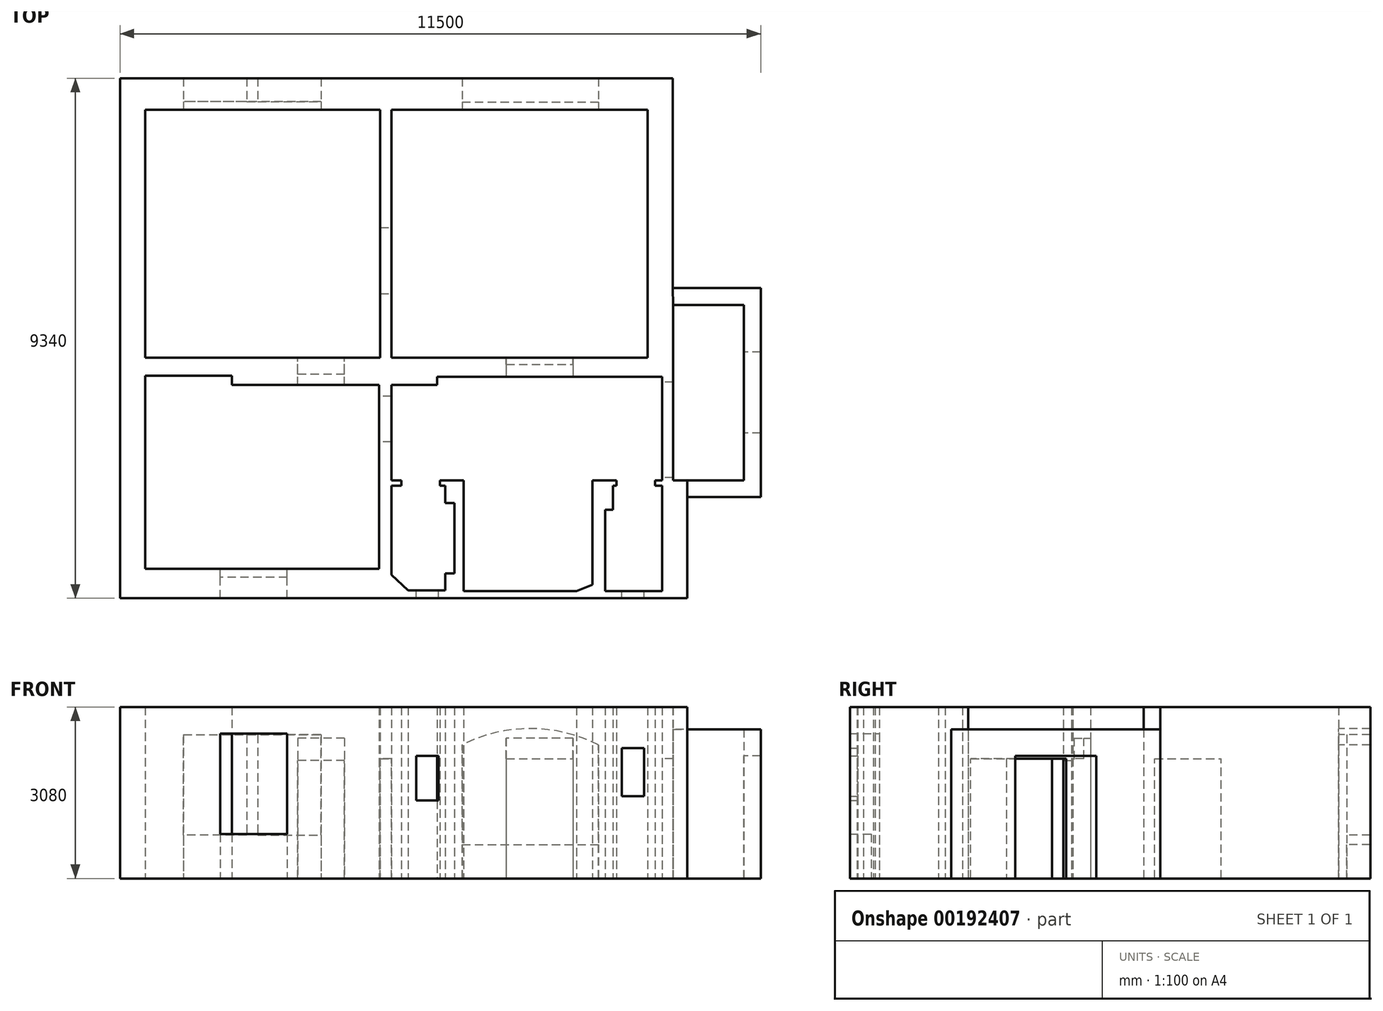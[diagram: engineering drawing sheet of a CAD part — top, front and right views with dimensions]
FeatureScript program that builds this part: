
annotation { "Feature Type Name" : "Feature", "Feature Type Description" : "" }
export const myFeature = defineFeature(function(context is Context, id is Id, definition is map)
    precondition{}
    {
        {
            var Q0;
            Q0=qCreatedBy(makeId("Top.planeOp"),FACE);
            var sketch = newSketch(context, id + "F0", { "sketchPlane" : qUnion([Q0])});
            skLineSegment(sketch, "E0.bottom", {"start": v(0, 0) * mm, "end": v(4600, 0) * mm});
            skLineSegment(sketch, "E0.top", {"start": v(0, 4450) * mm, "end": v(4600, 4450) * mm});
            skLineSegment(sketch, "E0.left", {"start": v(0, 0) * mm, "end": v(0, 4450) * mm});
            skLineSegment(sketch, "E0.right", {"start": v(4600, 0) * mm, "end": v(4600, 4450) * mm});
            skLineSegment(sketch, "E1.bottom", {"start": v(-200, 0) * mm, "end": v(-4420, 0) * mm});
            skLineSegment(sketch, "E1.top", {"start": v(-200, 4450) * mm, "end": v(-4420, 4450) * mm});
            skLineSegment(sketch, "E1.left", {"start": v(-200, 0) * mm, "end": v(-200, 4450) * mm});
            skLineSegment(sketch, "E1.right", {"start": v(-4420, 0) * mm, "end": v(-4420, 4450) * mm});
            skLineSegment(sketch, "E2", {"start": v(-220, -490) * mm, "end": v(-220, -3790) * mm});
            skLineSegment(sketch, "E3", {"start": v(-220, -3790) * mm, "end": v(-4420, -3790) * mm});
            skLineSegment(sketch, "E4", {"start": v(-4420, -3790) * mm, "end": v(-4420, -320) * mm});
            skLineSegment(sketch, "E5", {"start": v(-4420, -320) * mm, "end": v(-2860, -320) * mm});
            skLineSegment(sketch, "E6", {"start": v(-2860, -320) * mm, "end": v(-2860, -490) * mm});
            skLineSegment(sketch, "E7", {"start": v(-2860, -490) * mm, "end": v(-220, -490) * mm});
            skLineSegment(sketch, "E8", {"start": v(0, -490) * mm, "end": v(820, -490) * mm});
            skLineSegment(sketch, "E9", {"start": v(820, -490) * mm, "end": v(820, -340) * mm});
            skLineSegment(sketch, "E10", {"start": v(820, -340) * mm, "end": v(4860, -340) * mm});
            skLineSegment(sketch, "E11", {"start": v(4860, -340) * mm, "end": v(4860, -2200) * mm});
            skLineSegment(sketch, "E12", {"start": v(4860, -2200) * mm, "end": v(0, -2200) * mm});
            skLineSegment(sketch, "E13", {"start": v(0, -2200) * mm, "end": v(0, -490) * mm});
            skLineSegment(sketch, "E14", {"start": v(0, -2300) * mm, "end": v(0, -3900) * mm});
            skLineSegment(sketch, "E15", {"start": v(970, -3870) * mm, "end": v(1130, -3870) * mm});
            skLineSegment(sketch, "E16", {"start": v(1130, -3870) * mm, "end": v(1130, -2610) * mm});
            skLineSegment(sketch, "E17", {"start": v(1130, -2610) * mm, "end": v(970, -2610) * mm});
            skLineSegment(sketch, "E18", {"start": v(970, -2610) * mm, "end": v(970, -2300) * mm});
            skLineSegment(sketch, "E19", {"start": v(970, -2300) * mm, "end": v(0, -2300) * mm});
            skLineSegment(sketch, "E20", {"start": v(970, -3870) * mm, "end": v(970, -4180) * mm});
            skLineSegment(sketch, "E21", {"start": v(970, -4180) * mm, "end": v(300, -4180) * mm});
            skLineSegment(sketch, "E22", {"start": v(300, -4180) * mm, "end": v(0, -3900) * mm});
            skLineSegment(sketch, "E23", {"start": v(4860, -2300) * mm, "end": v(4860, -4190) * mm});
            skLineSegment(sketch, "E24", {"start": v(4860, -4190) * mm, "end": v(3840, -4190) * mm});
            skLineSegment(sketch, "E25", {"start": v(3840, -4190) * mm, "end": v(3840, -2730) * mm});
            skLineSegment(sketch, "E26", {"start": v(3840, -2730) * mm, "end": v(3980, -2730) * mm});
            skLineSegment(sketch, "E27", {"start": v(3980, -2730) * mm, "end": v(3980, -2300) * mm});
            skLineSegment(sketch, "E28", {"start": v(3980, -2300) * mm, "end": v(4860, -2300) * mm});
            skLineSegment(sketch, "E29", {"start": v(5050, 5020) * mm, "end": v(-4870, 5020) * mm});
            skLineSegment(sketch, "E30", {"start": v(-4870, 5020) * mm, "end": v(-4870, -4320) * mm});
            skLineSegment(sketch, "E31.bottom", {"start": v(5060, -2200) * mm, "end": v(6330, -2200) * mm});
            skLineSegment(sketch, "E31.top", {"start": v(5060, 950) * mm, "end": v(6330, 950) * mm});
            skLineSegment(sketch, "E31.left", {"start": v(5060, -2200) * mm, "end": v(5060, 950) * mm});
            skLineSegment(sketch, "E31.right", {"start": v(6330, -2200) * mm, "end": v(6330, 950) * mm});
            skLineSegment(sketch, "E32", {"start": v(4040, -2300) * mm, "end": v(4040, -2200) * mm});
            skLineSegment(sketch, "E33", {"start": v(4730, -2300) * mm, "end": v(4730, -2200) * mm});
            skLineSegment(sketch, "E34", {"start": v(3320.65, -4190) * mm, "end": v(1300, -4190) * mm});
            skLineSegment(sketch, "E35", {"start": v(1300, -4190) * mm, "end": v(1300, -2200) * mm});
            skLineSegment(sketch, "E36", {"start": v(180, -2200) * mm, "end": v(180, -2300) * mm});
            skLineSegment(sketch, "E37", {"start": v(870, -2200) * mm, "end": v(870, -2300) * mm});
            skLineSegment(sketch, "E38", {"start": v(3320.65, -4190) * mm, "end": v(3610, -4075.8) * mm});
            skLineSegment(sketch, "E39", {"start": v(3610, -4075.8) * mm, "end": v(3610, -2200) * mm});
            skLineSegment(sketch, "E40", {"start": v(-4870, -4320) * mm, "end": v(5310, -4320) * mm});
            skLineSegment(sketch, "E41", {"start": v(5310, -2500) * mm, "end": v(6630, -2500) * mm});
            skLineSegment(sketch, "E42", {"start": v(6630, -2500) * mm, "end": v(6630, 1250) * mm});
            skLineSegment(sketch, "E43", {"start": v(6630, 1250) * mm, "end": v(5050, 1250) * mm});
            skLineSegment(sketch, "E44", {"start": v(5050, 1250) * mm, "end": v(5050, 5020) * mm});
            skLineSegment(sketch, "E45", {"start": v(5310, -2500) * mm, "end": v(5310, -4320) * mm});
            skSolve(sketch);
        }
        {
            var Q0;
            Q0=makeQuery(id+"F0.imprint","IMPRINT",FACE,{"disambiguationData":[TD([[makeQuery(id+"F0.imprint","IMPRINT",EDGE,{"derivedFrom":sQuery(id+"F0.wireOp",EDGE,"E0.bottom")}),-1.0]])]});
            extrude(context, id + "F1", {"entities" : qUnion([Q0]), "depth" : 3080 * mm});
        }
        {
            var Q0;
            Q0=makeQuery(id+"F1.opExtrude","SWEPT_FACE",FACE,{"disambiguationData":[OSD([sQuery(id+"F0.wireOp",EDGE,"E10")])]});
            var sketch = newSketch(context, id + "F2", { "sketchPlane" : qUnion([Q0])});
            skLineSegment(sketch, "E46.bottom", {"start": v(2061.87, 2150) * mm, "end": v(3261.87, 2150) * mm});
            skLineSegment(sketch, "E46.top", {"start": v(2061.87, 0) * mm, "end": v(3261.87, 0) * mm});
            skLineSegment(sketch, "E46.left", {"start": v(2061.87, 2150) * mm, "end": v(2061.87, 0) * mm});
            skLineSegment(sketch, "E46.right", {"start": v(3261.87, 2150) * mm, "end": v(3261.87, 0) * mm});
            skSolve(sketch);
        }
        {
            var Q0;
            Q0=makeQuery(id+"F2.imprint","IMPRINT",FACE,{"disambiguationData":[TD([[makeQuery(id+"F2.imprint","IMPRINT",EDGE,{"derivedFrom":sQuery(id+"F2.wireOp",EDGE,"E46.bottom")}),-1.0]])]});
            extrude(context, id + "F3", {"entities" : qUnion([Q0]), "operationType" : NewBodyOperationType.REMOVE, "endBound" : BoundingType.UP_TO_NEXT, "oppositeDirection" : true, "depth" : 25 * mm});
        }
        {
            var Q0;
            Q0=makeQuery(id+"F1.opExtrude","SWEPT_FACE",FACE,{"disambiguationData":[OSD([sQuery(id+"F0.wireOp",EDGE,"E0.bottom")])]});
            var sketch = newSketch(context, id + "F4", { "sketchPlane" : qUnion([Q0])});
            skLineSegment(sketch, "E47.bottom", {"start": v(-3261.87, 2150) * mm, "end": v(-2061.87, 2150) * mm});
            skLineSegment(sketch, "E47.top", {"start": v(-3261.87, 2520) * mm, "end": v(-2061.87, 2520) * mm});
            skLineSegment(sketch, "E47.left", {"start": v(-3261.87, 2150) * mm, "end": v(-3261.87, 2520) * mm});
            skLineSegment(sketch, "E47.right", {"start": v(-2061.87, 2150) * mm, "end": v(-2061.87, 2520) * mm});
            skSolve(sketch);
        }
        {
            var Q0;
            Q0=makeQuery(id+"F4.imprint","IMPRINT",FACE,{"disambiguationData":[TD([[makeQuery(id+"F4.imprint","IMPRINT",EDGE,{"derivedFrom":sQuery(id+"F4.wireOp",EDGE,"E47.bottom")}),-1.0]])]});
            extrude(context, id + "F5", {"entities" : qUnion([Q0]), "operationType" : NewBodyOperationType.REMOVE, "oppositeDirection" : true, "depth" : 120 * mm});
        }
        {
            var Q0;
            Q0=makeQuery(id+"F1.opExtrude","SWEPT_FACE",FACE,{"disambiguationData":[OSD([sQuery(id+"F0.wireOp",EDGE,"E0.left")])]});
            var sketch = newSketch(context, id + "F6", { "sketchPlane" : qUnion([Q0])});
            skLineSegment(sketch, "E48.bottom", {"start": v(1150, 0) * mm, "end": v(2340, 0) * mm});
            skLineSegment(sketch, "E48.top", {"start": v(1150, 2150) * mm, "end": v(2340, 2150) * mm});
            skLineSegment(sketch, "E48.left", {"start": v(1150, 0) * mm, "end": v(1150, 2150) * mm});
            skLineSegment(sketch, "E48.right", {"start": v(2340, 0) * mm, "end": v(2340, 2150) * mm});
            skSolve(sketch);
        }
        {
            var Q0;
            Q0 = qSketchRegion(id + "F6", true);
            extrude(context, id + "F7", {"entities" : qUnion([Q0]), "operationType" : NewBodyOperationType.REMOVE, "endBound" : BoundingType.UP_TO_NEXT, "oppositeDirection" : true, "depth" : 25 * mm});
        }
        {
            var Q0;
            Q0=makeQuery(id+"F1.opExtrude","SWEPT_FACE",FACE,{"disambiguationData":[OSD([sQuery(id+"F0.wireOp",EDGE,"E31.right")])]});
            var sketch = newSketch(context, id + "F8", { "sketchPlane" : qUnion([Q0])});
            skLineSegment(sketch, "E49.bottom", {"start": v(1350, 0) * mm, "end": v(-100, 0) * mm});
            skLineSegment(sketch, "E49.top", {"start": v(1350, 2200) * mm, "end": v(-100, 2200) * mm});
            skLineSegment(sketch, "E49.left", {"start": v(1350, 0) * mm, "end": v(1350, 2200) * mm});
            skLineSegment(sketch, "E49.right", {"start": v(-100, 0) * mm, "end": v(-100, 2200) * mm});
            skSolve(sketch);
        }
        {
            var Q0;
            Q0 = qSketchRegion(id + "F8", true);
            extrude(context, id + "F9", {"entities" : qUnion([Q0]), "operationType" : NewBodyOperationType.REMOVE, "endBound" : BoundingType.UP_TO_NEXT, "oppositeDirection" : true, "depth" : 25 * mm});
        }
        {
            var Q0;
            Q0=makeQuery(id+"F1.opExtrude","SWEPT_FACE",FACE,{"disambiguationData":[OSD([sQuery(id+"F0.wireOp",EDGE,"E1.bottom")])]});
            var sketch = newSketch(context, id + "F10", { "sketchPlane" : qUnion([Q0])});
            skLineSegment(sketch, "E50.bottom", {"start": v(840, 2520) * mm, "end": v(1680, 2520) * mm});
            skLineSegment(sketch, "E50.top", {"start": v(840, 0) * mm, "end": v(1680, 0) * mm});
            skLineSegment(sketch, "E50.left", {"start": v(840, 2520) * mm, "end": v(840, 0) * mm});
            skLineSegment(sketch, "E50.right", {"start": v(1680, 2520) * mm, "end": v(1680, 0) * mm});
            skSolve(sketch);
        }
        {
            var Q0;
            Q0 = qSketchRegion(id + "F10", true);
            extrude(context, id + "F11", {"entities" : qUnion([Q0]), "operationType" : NewBodyOperationType.REMOVE, "oppositeDirection" : true, "depth" : 300 * mm});
        }
        {
            var Q0;
            Q0=makeQuery(id+"F11.boolean.opBoolean","COPY",FACE,{"derivedFrom":makeQuery(id+"F11.opExtrude","CAP_FACE",FACE,{"disambiguationData":[OSD([sQuery(id+"F10.wireOp",EDGE,"E50.bottom"),sQuery(id+"F10.wireOp",EDGE,"E50.top"),sQuery(id+"F10.wireOp",EDGE,"E50.left"),sQuery(id+"F10.wireOp",EDGE,"E50.right")])],"isStart":false})});
            var sketch = newSketch(context, id + "F12", { "sketchPlane" : qUnion([Q0])});
            skLineSegment(sketch, "E51.bottom", {"start": v(840, 2120) * mm, "end": v(1680, 2120) * mm});
            skLineSegment(sketch, "E51.top", {"start": v(840, 0) * mm, "end": v(1680, 0) * mm});
            skLineSegment(sketch, "E51.left", {"start": v(840, 2120) * mm, "end": v(840, 0) * mm});
            skLineSegment(sketch, "E51.right", {"start": v(1680, 2120) * mm, "end": v(1680, 0) * mm});
            skSolve(sketch);
        }
        {
            var Q0;
            Q0=makeQuery(id+"F12.imprint","IMPRINT",FACE,{"disambiguationData":[TD([[makeQuery(id+"F12.imprint","IMPRINT",EDGE,{"derivedFrom":sQuery(id+"F12.wireOp",EDGE,"E51.bottom")}),-1.0]])]});
            extrude(context, id + "F13", {"entities" : qUnion([Q0]), "operationType" : NewBodyOperationType.REMOVE, "endBound" : BoundingType.UP_TO_NEXT, "oppositeDirection" : true, "depth" : 25 * mm});
        }
        {
            var Q0;
            Q0=makeQuery(id+"F1.opExtrude","SWEPT_FACE",FACE,{"disambiguationData":[OSD([sQuery(id+"F0.wireOp",EDGE,"E2")])]});
            var sketch = newSketch(context, id + "F14", { "sketchPlane" : qUnion([Q0])});
            skLineSegment(sketch, "E52.bottom", {"start": v(690, 2150) * mm, "end": v(1510, 2150) * mm});
            skLineSegment(sketch, "E52.top", {"start": v(690, 0) * mm, "end": v(1510, 0) * mm});
            skLineSegment(sketch, "E52.left", {"start": v(690, 2150) * mm, "end": v(690, 0) * mm});
            skLineSegment(sketch, "E52.right", {"start": v(1510, 2150) * mm, "end": v(1510, 0) * mm});
            skSolve(sketch);
        }
        {
            var Q0;
            Q0 = qSketchRegion(id + "F14", true);
            extrude(context, id + "F15", {"entities" : qUnion([Q0]), "operationType" : NewBodyOperationType.REMOVE, "endBound" : BoundingType.UP_TO_NEXT, "oppositeDirection" : true, "depth" : 25 * mm});
        }
        {
            var Q0;
            Q0=makeQuery(id+"F1.opExtrude","SWEPT_FACE",FACE,{"disambiguationData":[OSD([sQuery(id+"F0.wireOp",EDGE,"E3")])]});
            var sketch = newSketch(context, id + "F16", { "sketchPlane" : qUnion([Q0])});
            skLineSegment(sketch, "E53.bottom", {"start": v(1870, 2600) * mm, "end": v(3070, 2600) * mm});
            skLineSegment(sketch, "E53.top", {"start": v(1870, 800) * mm, "end": v(3070, 800) * mm});
            skLineSegment(sketch, "E53.left", {"start": v(1870, 2600) * mm, "end": v(1870, 800) * mm});
            skLineSegment(sketch, "E53.right", {"start": v(3070, 2600) * mm, "end": v(3070, 800) * mm});
            skSolve(sketch);
        }
        {
            var Q0;
            Q0 = qSketchRegion(id + "F16", true);
            extrude(context, id + "F17", {"entities" : qUnion([Q0]), "operationType" : NewBodyOperationType.REMOVE, "endBound" : BoundingType.UP_TO_NEXT, "oppositeDirection" : true, "depth" : 25 * mm});
        }
        {
            var Q0;
            Q0=makeQuery(id+"F1.opExtrude","SWEPT_FACE",FACE,{"disambiguationData":[OSD([sQuery(id+"F0.wireOp",EDGE,"E1.top")])]});
            var sketch = newSketch(context, id + "F18", { "sketchPlane" : qUnion([Q0])});
            skLineSegment(sketch, "E54.bottom", {"start": v(-2395, 2580) * mm, "end": v(-1260, 2580) * mm});
            skLineSegment(sketch, "E54.top", {"start": v(-2395, 780) * mm, "end": v(-1260, 780) * mm});
            skLineSegment(sketch, "E54.left", {"start": v(-2395, 2580) * mm, "end": v(-2395, 780) * mm});
            skLineSegment(sketch, "E54.right", {"start": v(-1260, 2580) * mm, "end": v(-1260, 780) * mm});
            skLineSegment(sketch, "E55.bottom", {"start": v(-2595, 2580) * mm, "end": v(-3730, 2580) * mm});
            skLineSegment(sketch, "E55.top", {"start": v(-2595, 780) * mm, "end": v(-3730, 780) * mm});
            skLineSegment(sketch, "E55.left", {"start": v(-2595, 2580) * mm, "end": v(-2595, 780) * mm});
            skLineSegment(sketch, "E55.right", {"start": v(-3730, 2580) * mm, "end": v(-3730, 780) * mm});
            skSolve(sketch);
        }
        {
            var Q0;
            Q0 = qSketchRegion(id + "F18", true);
            extrude(context, id + "F19", {"entities" : qUnion([Q0]), "operationType" : NewBodyOperationType.REMOVE, "endBound" : BoundingType.UP_TO_NEXT, "oppositeDirection" : true, "depth" : 25 * mm});
        }
        {
            var Q0;
            Q0=makeQuery(id+"F1.opExtrude","SWEPT_FACE",FACE,{"disambiguationData":[OSD([sQuery(id+"F0.wireOp",EDGE,"E0.top")])]});
            var sketch = newSketch(context, id + "F20", { "sketchPlane" : qUnion([Q0])});
            skLineSegment(sketch, "E56", {"start": v(3720, 610) * mm, "end": v(1270, 610) * mm});
            skLineSegment(sketch, "E57", {"start": v(1270, 610) * mm, "end": v(1270, 2400) * mm});
            skLineSegment(sketch, "E58", {"start": v(3720, 610) * mm, "end": v(3720, 2400) * mm});
            skArc(sketch, "E59", {"start": v(3720, 2400) * mm, "mid": v(2495, 2690) * mm, "end": v(1270, 2400) * mm});
            skSolve(sketch);
        }
        {
            var Q0;
            Q0 = qSketchRegion(id + "F20", true);
            extrude(context, id + "F21", {"entities" : qUnion([Q0]), "operationType" : NewBodyOperationType.REMOVE, "endBound" : BoundingType.UP_TO_NEXT, "oppositeDirection" : true, "depth" : 25 * mm});
        }
        {
            var Q0;
            Q0=makeQuery(id+"F1.opExtrude","CAP_FACE",FACE,{"disambiguationData":[OSD([sQuery(id+"F0.wireOp",EDGE,"E0.bottom"),sQuery(id+"F0.wireOp",EDGE,"E0.top"),sQuery(id+"F0.wireOp",EDGE,"E0.left"),sQuery(id+"F0.wireOp",EDGE,"E0.right"),sQuery(id+"F0.wireOp",EDGE,"E1.bottom"),sQuery(id+"F0.wireOp",EDGE,"E1.top"),sQuery(id+"F0.wireOp",EDGE,"E1.left"),sQuery(id+"F0.wireOp",EDGE,"E1.right"),sQuery(id+"F0.wireOp",EDGE,"E2"),sQuery(id+"F0.wireOp",EDGE,"E3"),sQuery(id+"F0.wireOp",EDGE,"E4"),sQuery(id+"F0.wireOp",EDGE,"E5"),sQuery(id+"F0.wireOp",EDGE,"E6"),sQuery(id+"F0.wireOp",EDGE,"E7"),sQuery(id+"F0.wireOp",EDGE,"E8"),sQuery(id+"F0.wireOp",EDGE,"E9"),sQuery(id+"F0.wireOp",EDGE,"E10"),sQuery(id+"F0.wireOp",EDGE,"E11"),sQuery(id+"F0.wireOp",EDGE,"E12"),sQuery(id+"F0.wireOp",EDGE,"E13"),sQuery(id+"F0.wireOp",EDGE,"E14"),sQuery(id+"F0.wireOp",EDGE,"E15"),sQuery(id+"F0.wireOp",EDGE,"E16"),sQuery(id+"F0.wireOp",EDGE,"E17"),sQuery(id+"F0.wireOp",EDGE,"E18"),sQuery(id+"F0.wireOp",EDGE,"E19"),sQuery(id+"F0.wireOp",EDGE,"E20"),sQuery(id+"F0.wireOp",EDGE,"E21"),sQuery(id+"F0.wireOp",EDGE,"E22"),sQuery(id+"F0.wireOp",EDGE,"E23"),sQuery(id+"F0.wireOp",EDGE,"E24"),sQuery(id+"F0.wireOp",EDGE,"E25"),sQuery(id+"F0.wireOp",EDGE,"E26"),sQuery(id+"F0.wireOp",EDGE,"E27"),sQuery(id+"F0.wireOp",EDGE,"E28"),sQuery(id+"F0.wireOp",EDGE,"E29"),sQuery(id+"F0.wireOp",EDGE,"E30"),sQuery(id+"F0.wireOp",EDGE,"E31.bottom"),sQuery(id+"F0.wireOp",EDGE,"E31.top"),sQuery(id+"F0.wireOp",EDGE,"E31.left"),sQuery(id+"F0.wireOp",EDGE,"E31.right"),sQuery(id+"F0.wireOp",EDGE,"E32"),sQuery(id+"F0.wireOp",EDGE,"E33"),sQuery(id+"F0.wireOp",EDGE,"E34"),sQuery(id+"F0.wireOp",EDGE,"E35"),sQuery(id+"F0.wireOp",EDGE,"E36"),sQuery(id+"F0.wireOp",EDGE,"E37"),sQuery(id+"F0.wireOp",EDGE,"E38"),sQuery(id+"F0.wireOp",EDGE,"E39"),sQuery(id+"F0.wireOp",EDGE,"E40"),sQuery(id+"F0.wireOp",EDGE,"E41"),sQuery(id+"F0.wireOp",EDGE,"E42"),sQuery(id+"F0.wireOp",EDGE,"E43"),sQuery(id+"F0.wireOp",EDGE,"E44"),sQuery(id+"F0.wireOp",EDGE,"E45")])],"isStart":false});
            var sketch = newSketch(context, id + "F22", { "sketchPlane" : qUnion([Q0])});
            skLineSegment(sketch, "E60", {"start": v(5310, -2500) * mm, "end": v(5310, -2200) * mm});
            skLineSegment(sketch, "E61", {"start": v(5060, 950) * mm, "end": v(5050, 1250) * mm});
            skSolve(sketch);
        }
        {
            var Q0;
            Q0 = qSketchRegion(id + "F22", true);
            var Q1;
            {var subQ1=sQuery(id+"F22.wireOp",EDGE,"E60");Q1=makeQuery(id+"F22.imprint","IMPRINT",FACE,{"disambiguationData":[TD([[makeQuery(id+"F22.imprint","IMPRINT",EDGE,{"derivedFrom":subQ1}),-1.0]])]});}
            extrude(context, id + "F23", {"entities" : qUnion([Q0, Q1]), "operationType" : NewBodyOperationType.REMOVE, "oppositeDirection" : true, "depth" : 400 * mm});
        }
        {
            var Q0;
            Q0=makeQuery(id+"F1.opExtrude","SWEPT_FACE",FACE,{"disambiguationData":[OSD([sQuery(id+"F0.wireOp",EDGE,"E11")])]});
            var sketch = newSketch(context, id + "F24", { "sketchPlane" : qUnion([Q0])});
            skLineSegment(sketch, "E62.bottom", {"start": v(440, 2150) * mm, "end": v(2150, 2150) * mm});
            skLineSegment(sketch, "E62.top", {"start": v(440, 0) * mm, "end": v(2150, 0) * mm});
            skLineSegment(sketch, "E62.left", {"start": v(440, 2150) * mm, "end": v(440, 0) * mm});
            skLineSegment(sketch, "E62.right", {"start": v(2150, 2150) * mm, "end": v(2150, 0) * mm});
            skSolve(sketch);
        }
        {
            var Q0;
            Q0 = qSketchRegion(id + "F24", true);
            extrude(context, id + "F25", {"entities" : qUnion([Q0]), "operationType" : NewBodyOperationType.REMOVE, "endBound" : BoundingType.UP_TO_NEXT, "oppositeDirection" : true, "depth" : 25 * mm});
        }
        {
            var Q0;
            Q0=makeQuery(id+"F1.opExtrude","SWEPT_FACE",FACE,{"disambiguationData":[OSD([sQuery(id+"F0.wireOp",EDGE,"E21")])]});
            var sketch = newSketch(context, id + "F26", { "sketchPlane" : qUnion([Q0])});
            skLineSegment(sketch, "E63.bottom", {"start": v(-843.98, 2200) * mm, "end": v(-443.98, 2200) * mm});
            skLineSegment(sketch, "E63.top", {"start": v(-843.98, 1400) * mm, "end": v(-443.98, 1400) * mm});
            skLineSegment(sketch, "E63.left", {"start": v(-843.98, 2200) * mm, "end": v(-843.98, 1400) * mm});
            skLineSegment(sketch, "E63.right", {"start": v(-443.98, 2200) * mm, "end": v(-443.98, 1400) * mm});
            skSolve(sketch);
        }
        {
            var Q0;
            Q0 = qSketchRegion(id + "F26", true);
            extrude(context, id + "F27", {"entities" : qUnion([Q0]), "operationType" : NewBodyOperationType.REMOVE, "endBound" : BoundingType.UP_TO_NEXT, "oppositeDirection" : true, "depth" : 25 * mm});
        }
        {
            var Q0;
            Q0=makeQuery(id+"F1.opExtrude","SWEPT_FACE",FACE,{"disambiguationData":[OSD([sQuery(id+"F0.wireOp",EDGE,"E24")])]});
            var sketch = newSketch(context, id + "F28", { "sketchPlane" : qUnion([Q0])});
            skLineSegment(sketch, "E64.bottom", {"start": v(-4537.34, 2341.65) * mm, "end": v(-4138.92, 2341.65) * mm});
            skLineSegment(sketch, "E64.top", {"start": v(-4537.34, 1474.65) * mm, "end": v(-4138.92, 1474.65) * mm});
            skLineSegment(sketch, "E64.left", {"start": v(-4537.34, 2341.65) * mm, "end": v(-4537.34, 1474.65) * mm});
            skLineSegment(sketch, "E64.right", {"start": v(-4138.92, 2341.65) * mm, "end": v(-4138.92, 1474.65) * mm});
            skSolve(sketch);
        }
        {
            var Q0;
            Q0 = qSketchRegion(id + "F28", true);
            extrude(context, id + "F29", {"entities" : qUnion([Q0]), "operationType" : NewBodyOperationType.REMOVE, "endBound" : BoundingType.UP_TO_NEXT, "oppositeDirection" : true, "depth" : 25 * mm});
        }
        {
            var Q0;
            Q0=makeQuery(id+"F1.opExtrude","SWEPT_FACE",FACE,{"disambiguationData":[OSD([sQuery(id+"F0.wireOp",EDGE,"E1.top")])]});
            var sketch = newSketch(context, id + "F30", { "sketchPlane" : qUnion([Q0])});
            skLineSegment(sketch, "E65.bottom", {"start": v(-3730, 780) * mm, "end": v(-1260, 780) * mm});
            skLineSegment(sketch, "E65.top", {"start": v(-3730, 0) * mm, "end": v(-1260, 0) * mm});
            skLineSegment(sketch, "E65.left", {"start": v(-3730, 780) * mm, "end": v(-3730, 0) * mm});
            skLineSegment(sketch, "E65.right", {"start": v(-1260, 780) * mm, "end": v(-1260, 0) * mm});
            skLineSegment(sketch, "E66", {"start": v(-2595, 2580) * mm, "end": v(-2395, 2580) * mm});
            skSolve(sketch);
        }
        {
            var Q0;
            Q0=makeQuery(id+"F30.imprint","IMPRINT",FACE,{"disambiguationData":[TD([[makeQuery(id+"F30.imprint","IMPRINT",EDGE,{"derivedFrom":sQuery(id+"F30.wireOp",EDGE,"E65.top")}),-1.0]])]});
            var Q1;
            Q1=makeQuery(id+"F30.imprint","IMPRINT",FACE,{"disambiguationData":[TD([[makeQuery(id+"F30.imprint","IMPRINT",EDGE,{"derivedFrom":sQuery(id+"F30.wireOp",EDGE,"E66")}),-1.0]])]});
            extrude(context, id + "F31", {"entities" : qUnion([Q0, Q1]), "operationType" : NewBodyOperationType.REMOVE, "oppositeDirection" : true, "depth" : 150 * mm});
        }
        {
            var Q0;
            Q0=makeQuery(id+"F1.opExtrude","SWEPT_FACE",FACE,{"disambiguationData":[OSD([sQuery(id+"F0.wireOp",EDGE,"E0.top")])]});
            var sketch = newSketch(context, id + "F32", { "sketchPlane" : qUnion([Q0])});
            skLineSegment(sketch, "E67.bottom", {"start": v(1270, 610) * mm, "end": v(3720, 610) * mm});
            skLineSegment(sketch, "E67.top", {"start": v(1270, 0) * mm, "end": v(3720, 0) * mm});
            skLineSegment(sketch, "E67.left", {"start": v(1270, 610) * mm, "end": v(1270, 0) * mm});
            skLineSegment(sketch, "E67.right", {"start": v(3720, 610) * mm, "end": v(3720, 0) * mm});
            skSolve(sketch);
        }
        {
            var Q0;
            Q0 = qSketchRegion(id + "F32", true);
            var Q1;
            Q1=makeQuery(id+"F32.imprint","IMPRINT",FACE,{"disambiguationData":[TD([[makeQuery(id+"F32.imprint","IMPRINT",EDGE,{"derivedFrom":sQuery(id+"F32.wireOp",EDGE,"E67.bottom")}),1.0]])]});
            extrude(context, id + "F33", {"entities" : qUnion([Q0, Q1]), "operationType" : NewBodyOperationType.REMOVE, "oppositeDirection" : true, "depth" : 140 * mm});
        }
        {
            var Q0;
            Q0=makeQuery(id+"F1.opExtrude","SWEPT_FACE",FACE,{"disambiguationData":[OSD([sQuery(id+"F0.wireOp",EDGE,"E3")])]});
            var sketch = newSketch(context, id + "F34", { "sketchPlane" : qUnion([Q0])});
            skLineSegment(sketch, "E68.bottom", {"start": v(1870, 800) * mm, "end": v(3070, 800) * mm});
            skLineSegment(sketch, "E68.top", {"start": v(1870, 0) * mm, "end": v(3070, 0) * mm});
            skLineSegment(sketch, "E68.left", {"start": v(1870, 800) * mm, "end": v(1870, 0) * mm});
            skLineSegment(sketch, "E68.right", {"start": v(3070, 800) * mm, "end": v(3070, 0) * mm});
            skSolve(sketch);
        }
        {
            var Q0;
            Q0 = qSketchRegion(id + "F34", true);
            extrude(context, id + "F35", {"entities" : qUnion([Q0]), "operationType" : NewBodyOperationType.REMOVE, "oppositeDirection" : true, "depth" : 150 * mm});
        }
    });
